FCSTD DOCUMENT  (FreeCAD 0.16R6706 (Git))
Label: KNX_2Taster_mit_Display_Unterbau_CCS
License: All rights reserved
LicenseURL: http://en.wikipedia.org/wiki/All_rights_reserved
objects: Sketcher::SketchObject×1
note: 1 computed .brp shape members not serialized (recipe doc carries the construction recipe); baked Part::Feature solids carry a one-line shape summary decoded from their .brp

FEATURE [Sketcher::SketchObject] Sketch
  sketch-geometry (31):
    g0: LineSegment StartX=1.83361 StartY=19.5301 StartZ=0 EndX=26.9336 EndY=19.5301 EndZ=0
    g1: LineSegment StartX=26.9336 StartY=19.5301 StartZ=0 EndX=26.9336 EndY=5.43009 EndZ=0
    g2: LineSegment StartX=32.9336 StartY=19.5301 StartZ=0 EndX=32.9336 EndY=5.43009 EndZ=0
    g3: LineSegment StartX=32.9336 StartY=19.5301 StartZ=0 EndX=58.0336 EndY=19.5301 EndZ=0
    g4: LineSegment StartX=58.0336 StartY=19.5301 StartZ=0 EndX=58.0336 EndY=57.1301 EndZ=0
    g5: LineSegment StartX=1.83361 StartY=57.1301 StartZ=0 EndX=1.83361 EndY=19.5301 EndZ=0
    g6: LineSegment StartX=3.33361 StartY=58.6301 StartZ=0 EndX=56.5336 EndY=58.6301 EndZ=0
    g7: ArcOfCircle CenterX=3.33361 CenterY=57.1301 CenterZ=0 NormalX=0 NormalY=0 NormalZ=1 Radius=1.5 StartAngle=1.5708 EndAngle=3.14159
    g8: ArcOfCircle CenterX=56.5336 CenterY=57.1301 CenterZ=0 NormalX=0 NormalY=0 NormalZ=1 Radius=1.5 StartAngle=6.28319 EndAngle=7.85398
    g9: LineSegment StartX=56.4556 StartY=1.73009 StartZ=0 EndX=44.9336 EndY=2.33009 EndZ=0
    g10: LineSegment StartX=44.9336 StartY=2.33009 StartZ=0 EndX=14.9336 EndY=2.33009 EndZ=0
    g11: LineSegment StartX=14.9336 StartY=2.33009 StartZ=0 EndX=3.41162 EndY=1.73009 EndZ=0
    g12: LineSegment [constr] StartX=3.41162 StartY=1.73009 StartZ=0 EndX=56.4556 EndY=1.73009 EndZ=0
    g13: LineSegment StartX=58.0336 StartY=5.23009 StartZ=0 EndX=58.0336 EndY=3.22806 EndZ=0
    g14: ArcOfCircle CenterX=56.5336 CenterY=3.22806 CenterZ=0 NormalX=0 NormalY=0 NormalZ=1 Radius=1.5 StartAngle=4.66036 EndAngle=6.28319
    g15: LineSegment StartX=1.83361 StartY=5.23009 StartZ=0 EndX=1.83361 EndY=3.22806 EndZ=0
    g16: ArcOfCircle CenterX=3.33361 CenterY=3.22806 CenterZ=0 NormalX=0 NormalY=0 NormalZ=1 Radius=1.5 StartAngle=3.14159 EndAngle=4.76442
    g17: LineSegment StartX=7.43361 StartY=57.2301 StartZ=0 EndX=52.4336 EndY=57.2301 EndZ=0
    g18: LineSegment StartX=52.4336 StartY=57.2301 StartZ=0 EndX=52.4336 EndY=22.2301 EndZ=0
    g19: LineSegment StartX=52.4336 StartY=22.2301 StartZ=0 EndX=35.4336 EndY=22.2301 EndZ=0
    g20: LineSegment StartX=7.43361 StartY=57.2301 StartZ=0 EndX=7.43361 EndY=22.2301 EndZ=0
    g21: LineSegment StartX=7.43361 StartY=22.2301 StartZ=0 EndX=24.4336 EndY=22.2301 EndZ=0
    g22: LineSegment StartX=24.4336 StartY=22.2301 StartZ=0 EndX=24.4336 EndY=21.6301 EndZ=0
    g23: LineSegment StartX=35.4336 StartY=22.2301 StartZ=0 EndX=35.4336 EndY=21.6301 EndZ=0
    g24: LineSegment StartX=35.4336 StartY=21.6301 StartZ=0 EndX=24.4336 EndY=21.6301 EndZ=0
    g25: LineSegment StartX=32.9336 StartY=5.43009 StartZ=0 EndX=44.9336 EndY=5.43009 EndZ=0
    g26: LineSegment StartX=44.9336 StartY=5.43009 StartZ=0 EndX=58.0336 EndY=5.23009 EndZ=0
    g27: LineSegment [constr] StartX=44.9336 StartY=5.43009 StartZ=0 EndX=44.9336 EndY=2.33009 EndZ=0
    g28: LineSegment StartX=26.9336 StartY=5.43009 StartZ=0 EndX=14.9336 EndY=5.43009 EndZ=0
    g29: LineSegment StartX=14.9336 StartY=5.43009 StartZ=0 EndX=1.83361 EndY=5.23009 EndZ=0
    g30: LineSegment [constr] StartX=14.9336 StartY=5.43009 StartZ=0 EndX=14.9336 EndY=2.33009 EndZ=0
  constraints (93):
    c: Horizontal(g0)
    c: Coincident(g1,g0)
    c: Vertical(g1)
    c: Vertical(g2)
    c: Coincident(g3,g2)
    c: Horizontal(g3)
    c: Coincident(g4,g3)
    c: Vertical(g4)
    c: Coincident(g5,g0)
    c: Vertical(g5)
    c: Horizontal(g6)
    c: DistanceX(g5,g4) = 56.2
    c: Coincident(g7,g5)
    c: Coincident(g8,g6)
    c: Coincident(g8,g4)
    c: Coincident(g6,g7)
    c: Tangent(g7,g6)
    c: Tangent(g5,g7)
    c: Tangent(g6,g8)
    c: Tangent(g4,g8)
    c: Radius(g8) = 1.5
    c: Equal(g8,g7)
    c: DistanceX(g0,g0) = 25.1
    c: DistanceX(g3,g3) = 25.1
    c: DistanceY(g2,g2) = 14.1
    c: Coincident(g10,g9)
    c: Horizontal(g10)
    c: Coincident(g11,g10)
    c: DistanceY(g9,g6) = 56.9
    c: Coincident(g12,g11)
    c: Coincident(g12,g9)
    c: Horizontal(g12)
    c: DistanceY(g9,g2) = 3.1
    c: DistanceY(g3,g6) = 39.1
    c: DistanceX(g9,g13) = 13.1
    c: DistanceX(g10,g10) = 30
    c: Vertical(g13)
    c: Coincident(g14,g13)
    c: Coincident(g14,g9)
    c: Tangent(g14,g13)
    c: Tangent(g14,g9)
    c: Equal(g14,g8)
    c: Vertical(g15)
    c: Coincident(g16,g15)
    c: Coincident(g16,g11)
    c: Tangent(g16,g15)
    c: Tangent(g16,g11)
    c: Equal(g16,g8)
    c: Horizontal(g17)
    c: Coincident(g18,g17)
    c: Vertical(g18)
    c: Coincident(g19,g18)
    c: Horizontal(g19)
    c: Coincident(g20,g17)
    c: Vertical(g20)
    c: Coincident(g21,g20)
    c: Horizontal(g21)
    c: Coincident(g22,g21)
    c: Equal(g20,g18)
    c: DistanceY(g18,g18) = 35
    c: Vertical(g22)
    c: Coincident(g24,g22)
    c: Horizontal(g24)
    c: Coincident(g23,g24)
    c: Vertical(g23)
    c: DistanceX(g17,g17) = 45
    c: Equal(g21,g19)
    c: DistanceX(g21,g21) = 17
    c: Coincident(g19,g23)
    c: Equal(g23,g22)
    c: DistanceY(g23,g23) = 0.6
    c: DistanceX(g17,g4) = 5.6
    c: Coincident(g25,g2)
    c: Horizontal(g25)
    c: Coincident(g26,g13)
    c: Coincident(g27,g25)
    c: Coincident(g27,g9)
    c: Vertical(g27)
    c: Coincident(g25,g26)
    c: DistanceY(g13,g3) = 14.3
    c: Coincident(g28,g1)
    c: Horizontal(g28)
    c: Coincident(g29,g28)
    c: Coincident(g29,g15)
    c: Coincident(g30,g28)
    c: Coincident(g30,g10)
    c: Vertical(g30)
    c: DistanceX(g29,g29) = 13.1
    c: DistanceY(g15,g0) = 14.3
    c: Equal(g1,g2)
    c: Equal(g5,g4)
    c: DistanceX(g2,g13) = 25.1
    c: DistanceY(g17,g6) = 1.4
